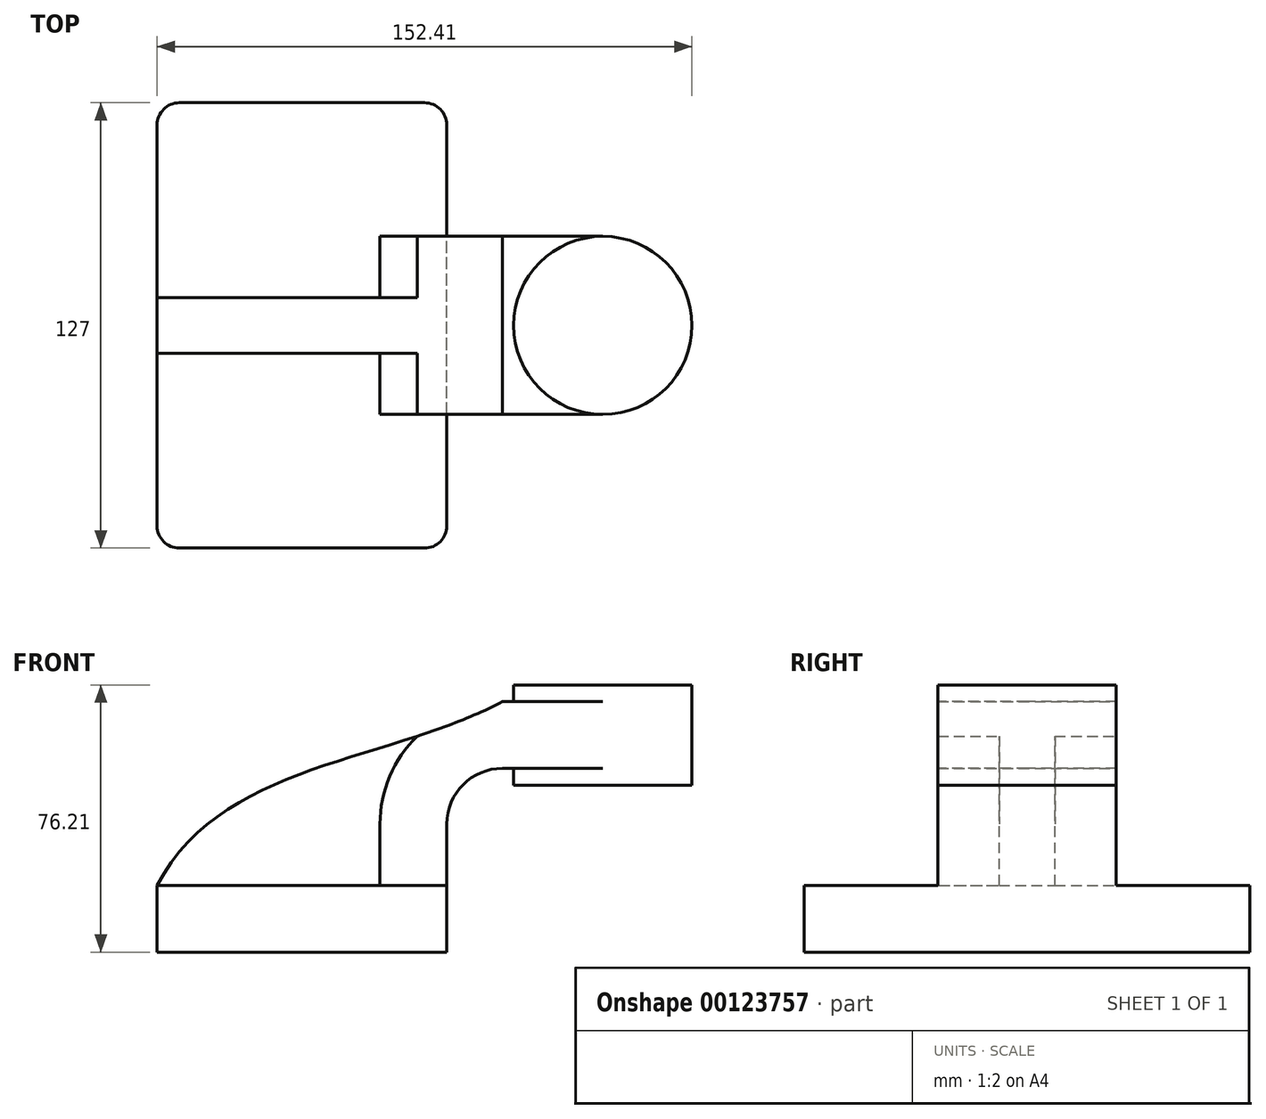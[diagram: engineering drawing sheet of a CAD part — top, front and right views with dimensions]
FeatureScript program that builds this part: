
annotation { "Feature Type Name" : "Feature", "Feature Type Description" : "" }
export const myFeature = defineFeature(function(context is Context, id is Id, definition is map)
    precondition{}
    {
        {
            var Q0;
            Q0=qCreatedBy(makeId("Front.planeOp"),FACE);
            var sketch = newSketch(context, id + "F0", { "sketchPlane" : qUnion([Q0])});
            skLineSegment(sketch, "E0.bottom", {"start": v(41.27, 9.53) * mm, "end": v(-41.28, 9.53) * mm});
            skLineSegment(sketch, "E0.top", {"start": v(41.28, -9.52) * mm, "end": v(-41.27, -9.52) * mm});
            skLineSegment(sketch, "E0.left", {"start": v(41.28, 9.53) * mm, "end": v(41.28, -9.52) * mm});
            skLineSegment(sketch, "E0.right", {"start": v(-41.28, 9.53) * mm, "end": v(-41.27, -9.52) * mm});
            skPoint(sketch, "E0.middle", {"position": v(0, 0) * mm});
            skLineSegment(sketch, "E1.bottom", {"start": v(60.32, 38.1) * mm, "end": v(111.12, 38.1) * mm});
            skLineSegment(sketch, "E1.top", {"start": v(60.32, 66.68) * mm, "end": v(111.12, 66.68) * mm});
            skLineSegment(sketch, "E1.left", {"start": v(60.32, 38.1) * mm, "end": v(60.32, 66.68) * mm});
            skLineSegment(sketch, "E1.right", {"start": v(111.12, 38.1) * mm, "end": v(111.12, 66.68) * mm});
            skPoint(sketch, "E1.middle", {"position": v(85.72, 52.39) * mm});
            skLineSegment(sketch, "E2", {"start": v(41.27, 9.53) * mm, "end": v(41.27, 27) * mm});
            skArc(sketch, "E3", {"start": v(41.27, 27) * mm, "mid": v(45.92, 38.23) * mm, "end": v(57.15, 42.88) * mm});
            skLineSegment(sketch, "E4", {"start": v(57.15, 42.88) * mm, "end": v(85.72, 42.88) * mm});
            skLineSegment(sketch, "E5.0", {"start": v(57.15, 61.93) * mm, "end": v(85.72, 61.93) * mm});
            skArc(sketch, "E5.1", {"start": v(22.23, 27) * mm, "mid": v(32.45, 51.7) * mm, "end": v(57.15, 61.93) * mm});
            skLineSegment(sketch, "E5.2", {"start": v(22.22, 9.53) * mm, "end": v(22.22, 27) * mm});
            skLineSegment(sketch, "E6", {"start": v(85.72, 38.1) * mm, "end": v(85.72, 66.68) * mm});
            skFitSpline(sketch, "E7", {"points": [v(-41.28, 9.53) * mm, v(57.15, 61.93) * mm], "startDerivative": vector(54.95, 105.3) * mm, "endDerivative": vector(98.42, 52.4) * mm});
            skSolve(sketch);
        }
        {
            var Q0;
            Q0=makeQuery(id+"F0.imprint","IMPRINT",FACE,{"disambiguationData":[TD([[makeQuery(id+"F0.imprint","IMPRINT",EDGE,{"derivedFrom":sQuery(id+"F0.wireOp",EDGE,"E0.top")}),-1.0]])]});
            extrude(context, id + "F1", {"entities" : qUnion([Q0]), "endBound" : BoundingType.SYMMETRIC, "depth" : 127 * mm});
        }
        {
            var Q0;
            {var subQ0=sQuery(id+"F0.wireOp",EDGE,"E4");var subQ1=sQuery(id+"F0.wireOp",EDGE,"E1.left");var subQ2=makeQuery(id+"F0.imprint","INTERSECT",VERTEX,{"derivedFrom":[subQ1,subQ0]});Q0=makeQuery(id+"F0.imprint","IMPRINT",FACE,{"disambiguationData":[TD([[makeQuery(id+"F0.imprint","IMPRINT",EDGE,{"disambiguationData":[TD([[subQ2,-1.0]])],"derivedFrom":subQ1}),-1.0]])]});}
            var Q1;
            {var subQ1=sQuery(id+"F0.wireOp",EDGE,"E2");Q1=makeQuery(id+"F0.imprint","IMPRINT",FACE,{"disambiguationData":[TD([[makeQuery(id+"F0.imprint","IMPRINT",EDGE,{"derivedFrom":subQ1}),1.0]])]});}
            extrude(context, id + "F2", {"entities" : qUnion([Q0, Q1]), "operationType" : NewBodyOperationType.ADD, "endBound" : BoundingType.SYMMETRIC, "depth" : 50.8 * mm});
        }
        {
            var Q0;
            {var subQ3=sQuery(id+"F0.wireOp",EDGE,"E5.2");Q0=makeQuery(id+"F0.imprint","IMPRINT",FACE,{"disambiguationData":[TD([[makeQuery(id+"F0.imprint","IMPRINT",EDGE,{"derivedFrom":subQ3}),1.0]])]});}
            extrude(context, id + "F3", {"entities" : qUnion([Q0]), "operationType" : NewBodyOperationType.ADD, "endBound" : BoundingType.SYMMETRIC, "depth" : 15.88 * mm});
        }
        {
            var Q0;
            {var subQ0=sQuery(id+"F0.wireOp",EDGE,"E1.right");Q0=makeQuery(id+"F0.imprint","IMPRINT",FACE,{"disambiguationData":[TD([[makeQuery(id+"F0.imprint","IMPRINT",EDGE,{"derivedFrom":subQ0}),1.0]])]});}
            var Q1;
            Q1=sQuery(id+"F0.wireOp",EDGE,"E6");
            revolve(context, id + "F4", {"operationType" : NewBodyOperationType.ADD, "entities" : qUnion([Q0]), "axis" : qUnion([Q1]), "revolveType" : RevolveType.FULL});
        }
        {
            var Q0;
            Q0=makeQuery(id+"F1.opExtrude","CAP_EDGE",EDGE,{"disambiguationData":[OSD([sQuery(id+"F0.wireOp",EDGE,"E0.right")])],"isStart":false});
            var Q1;
            Q1=makeQuery(id+"F1.opExtrude","CAP_EDGE",EDGE,{"disambiguationData":[OSD([sQuery(id+"F0.wireOp",EDGE,"E0.left")])],"isStart":false});
            var Q2;
            Q2=makeQuery(id+"F1.opExtrude","CAP_EDGE",EDGE,{"disambiguationData":[OSD([sQuery(id+"F0.wireOp",EDGE,"E0.left")])],"isStart":true});
            var Q3;
            Q3=makeQuery(id+"F1.opExtrude","CAP_EDGE",EDGE,{"disambiguationData":[OSD([sQuery(id+"F0.wireOp",EDGE,"E0.right")])],"isStart":true});
            fillet(context, id + "F5", {"entities" : qUnion([Q0, Q1, Q2, Q3]), "radius" : 6.35 * mm, "tangentPropagation" : true, "allowEdgeOverflow" : false});
        }
    });
